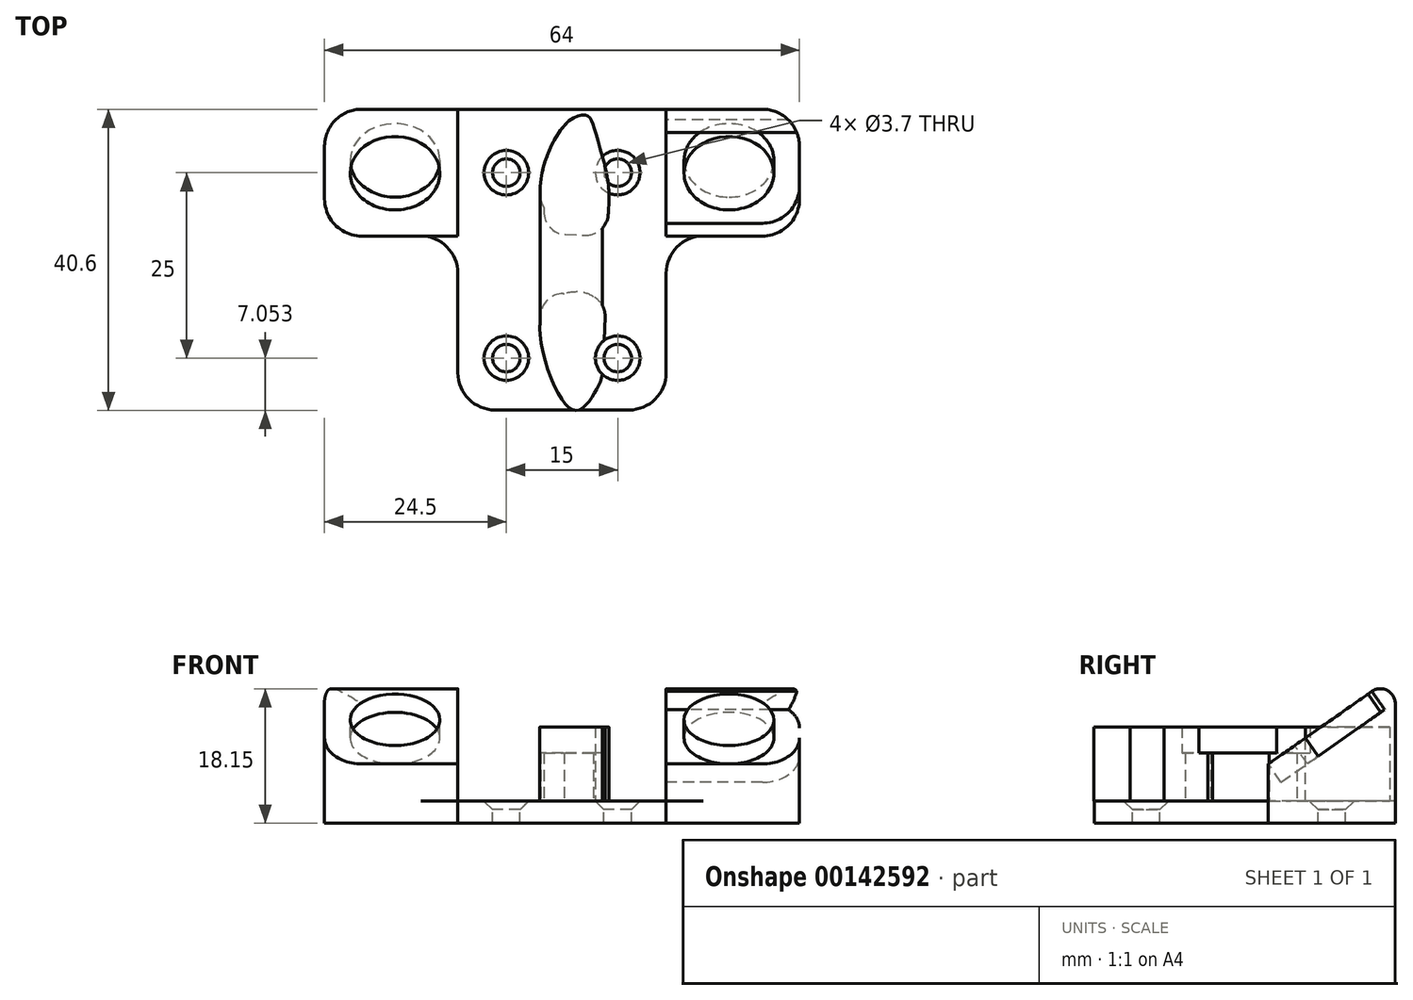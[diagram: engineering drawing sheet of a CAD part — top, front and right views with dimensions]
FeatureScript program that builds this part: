
annotation { "Feature Type Name" : "Feature", "Feature Type Description" : "" }
export const myFeature = defineFeature(function(context is Context, id is Id, definition is map)
    precondition{}
    {
        {
            var Q0;
            Q0=qCreatedBy(makeId("Top.planeOp"),FACE);
            var sketch = newSketch(context, id + "F0", { "sketchPlane" : qUnion([Q0])});
            skLineSegment(sketch, "E0.rect.top", {"start": v(-9.03, -25.17) * mm, "end": v(9.03, -25.17) * mm});
            skPoint(sketch, "E0.rect.middle", {"position": v(0, 0) * mm});
            skLineSegment(sketch, "E1.rect.bottom", {"start": v(27, 15.36) * mm, "end": v(-27, 15.36) * mm});
            skLineSegment(sketch, "E1.rect.top", {"start": v(27, -1.74) * mm, "end": v(19.03, -1.74) * mm});
            skLineSegment(sketch, "E1.rect.left", {"start": v(32, 15.36) * mm, "end": v(32, 15.36) * mm});
            skLineSegment(sketch, "E1.rect.right", {"start": v(-32, 10.36) * mm, "end": v(-32, 3.26) * mm});
            skPoint(sketch, "E1.rect.middle", {"position": v(0, 6.81) * mm});
            skLineSegment(sketch, "E2.trimOffspring", {"start": v(-19.03, -1.74) * mm, "end": v(-27, -1.74) * mm});
            skLineSegment(sketch, "E3", {"start": v(0, 6.81) * mm, "end": v(0, -18.19) * mm, "construction": true});
            skPoint(sketch, "E3.endSnap0", {"position": v(0, -25.17) * mm});
            skLineSegment(sketch, "E4", {"start": v(0, 6.81) * mm, "end": v(32, 6.81) * mm, "construction": true});
            skLineSegment(sketch, "E5", {"start": v(0, 6.81) * mm, "end": v(-32, 6.81) * mm, "construction": true});
            skPoint(sketch, "E6", {"position": v(7.5, 6.81) * mm});
            skLineSegment(sketch, "E7", {"start": v(7.5, 6.81) * mm, "end": v(7.5, -18.19) * mm, "construction": true});
            skPoint(sketch, "E8", {"position": v(7.5, -18.19) * mm});
            skPoint(sketch, "E9.MirrorP", {"position": v(-7.5, -18.19) * mm});
            skPoint(sketch, "E10.MirrorP", {"position": v(-7.5, 6.81) * mm});
            skCircle(sketch, "E11", {"center": v(-22.5, 6.81) * mm, "radius": 6.05 * mm, "construction": true});
            skCircle(sketch, "E12", {"center": v(22.5, 6.72) * mm, "radius": 6.05 * mm, "construction": true});
            skLineSegment(sketch, "E13", {"start": v(-7.5, 6.81) * mm, "end": v(-7.5, -18.19) * mm, "construction": true});
            skLineSegment(sketch, "E14", {"start": v(-7.5, -18.19) * mm, "end": v(7.5, -18.19) * mm, "construction": true});
            skPoint(sketch, "E15.orphan", {"position": v(0, -14.27) * mm});
            skPoint(sketch, "E16.orphan", {"position": v(0, 15.36) * mm});
            skLineSegment(sketch, "E17", {"start": v(14.03, -20.17) * mm, "end": v(14.03, -6.74) * mm});
            skLineSegment(sketch, "E18.MirrorCS", {"start": v(-14.03, -20.17) * mm, "end": v(-14.03, -6.74) * mm});
            skPoint(sketch, "E19.orphan", {"position": v(18, -25.17) * mm});
            skPoint(sketch, "E20.orphan", {"position": v(-18, -25.17) * mm});
            skLineSegment(sketch, "E21", {"start": v(14.03, -6.74) * mm, "end": v(14.03, 15.36) * mm});
            skLineSegment(sketch, "E22", {"start": v(32, -1.74) * mm, "end": v(32, -1.74) * mm});
            skLineSegment(sketch, "E23", {"start": v(32, 10.36) * mm, "end": v(32, 3.26) * mm});
            skLineSegment(sketch, "E24", {"start": v(14.03, 15.36) * mm, "end": v(14.03, 15.36) * mm});
            skLineSegment(sketch, "E25", {"start": v(-14.03, 15.36) * mm, "end": v(-14.03, 15.36) * mm});
            skLineSegment(sketch, "E26", {"start": v(-14.03, -6.74) * mm, "end": v(-14.03, 15.36) * mm});
            skLineSegment(sketch, "E27", {"start": v(-32, -1.74) * mm, "end": v(-32, -1.74) * mm});
            skLineSegment(sketch, "E28", {"start": v(-32, 15.36) * mm, "end": v(-32, 15.36) * mm});
            skArc(sketch, "E29.filletArc", {"start": v(19.03, -1.74) * mm, "mid": v(15.5, -3.2) * mm, "end": v(14.03, -6.74) * mm});
            skArc(sketch, "E30.filletArc", {"start": v(-14.03, -6.74) * mm, "mid": v(-15.5, -3.2) * mm, "end": v(-19.03, -1.74) * mm});
            skPoint(sketch, "E31.visualSharp", {"position": v(-14.03, -25.17) * mm});
            skArc(sketch, "E31.filletArc", {"start": v(-14.03, -20.17) * mm, "mid": v(-12.57, -23.7) * mm, "end": v(-9.03, -25.17) * mm});
            skPoint(sketch, "E32.visualSharp", {"position": v(14.03, -25.17) * mm});
            skArc(sketch, "E32.filletArc", {"start": v(9.03, -25.17) * mm, "mid": v(12.57, -23.7) * mm, "end": v(14.03, -20.17) * mm});
            skPoint(sketch, "E33.visualSharp", {"position": v(32, -1.74) * mm});
            skArc(sketch, "E33.filletArc", {"start": v(27, -1.74) * mm, "mid": v(30.54, -0.27) * mm, "end": v(32, 3.26) * mm});
            skPoint(sketch, "E34.visualSharp", {"position": v(32, 15.36) * mm});
            skArc(sketch, "E34.filletArc", {"start": v(32, 10.36) * mm, "mid": v(30.54, 13.9) * mm, "end": v(27, 15.36) * mm});
            skPoint(sketch, "E35.visualSharp", {"position": v(-32, 15.36) * mm});
            skArc(sketch, "E35.filletArc", {"start": v(-27, 15.36) * mm, "mid": v(-30.54, 13.9) * mm, "end": v(-32, 10.36) * mm});
            skPoint(sketch, "E36.visualSharp", {"position": v(-32, -1.74) * mm});
            skArc(sketch, "E36.filletArc", {"start": v(-32, 3.26) * mm, "mid": v(-30.54, -0.27) * mm, "end": v(-27, -1.74) * mm});
            skPoint(sketch, "E37.orphan", {"position": v(-14.03, -4.9) * mm});
            skPoint(sketch, "E38.orphan", {"position": v(14.03, -4.9) * mm});
            skLineSegment(sketch, "E39", {"start": v(-20.86, -1.74) * mm, "end": v(21.69, -1.74) * mm});
            skSolve(sketch);
        }
        {
            var Q0;
            Q0=makeQuery(id+"F0.imprint","IMPRINT",FACE,{"disambiguationData":[TD([[makeQuery(id+"F0.imprint","IMPRINT",EDGE,{"derivedFrom":sQuery(id+"F0.wireOp",EDGE,"E1.rect.right")}),1.0]])]});
            var Q1;
            Q1=makeQuery(id+"F0.imprint","IMPRINT",FACE,{"disambiguationData":[TD([[makeQuery(id+"F0.imprint","IMPRINT",EDGE,{"derivedFrom":sQuery(id+"F0.wireOp",EDGE,"E0.rect.top")}),1.0]])]});
            var Q2;
            Q2=makeQuery(id+"F0.imprint","IMPRINT",FACE,{"disambiguationData":[TD([[makeQuery(id+"F0.imprint","IMPRINT",EDGE,{"derivedFrom":sQuery(id+"F0.wireOp",EDGE,"E1.rect.top")}),-1.0]])]});
            var Q3;
            {var subQ0=sQuery(id+"F0.wireOp",EDGE,"E21");var subQ1=sQuery(id+"F0.wireOp",EDGE,"E1.rect.bottom");var subQ2=makeQuery(id+"F0.imprint","INTERSECT",VERTEX,{"derivedFrom":[subQ1,subQ0]});Q3=makeQuery(id+"F0.imprint","IMPRINT",FACE,{"disambiguationData":[TD([[makeQuery(id+"F0.imprint","IMPRINT",EDGE,{"disambiguationData":[TD([[subQ2,-1.0]])],"derivedFrom":subQ1}),1.0]])]});}
            var Q4;
            {var subQ0=sQuery(id+"F0.wireOp",EDGE,"E30.filletArc");Q4=makeQuery(id+"F0.imprint","IMPRINT",FACE,{"disambiguationData":[TD([[makeQuery(id+"F0.imprint","IMPRINT",EDGE,{"derivedFrom":subQ0}),-1.0]])]});}
            var Q5;
            {var subQ0=sQuery(id+"F0.wireOp",EDGE,"E29.filletArc");Q5=makeQuery(id+"F0.imprint","IMPRINT",FACE,{"disambiguationData":[TD([[makeQuery(id+"F0.imprint","IMPRINT",EDGE,{"derivedFrom":subQ0}),-1.0]])]});}
            extrude(context, id + "F1", {"entities" : qUnion([Q0, Q1, Q2, Q3, Q4, Q5]), "depth" : 3 * mm});
        }
        {
            var Q0;
            Q0=qCreatedBy(makeId("Right.planeOp"),FACE);
            var sketch = newSketch(context, id + "F2", { "sketchPlane" : qUnion([Q0])});
            skLineSegment(sketch, "E40.0", {"start": v(-1.74, 3) * mm, "end": v(-1.74, 0) * mm});
            skLineSegment(sketch, "E41.0", {"start": v(15.36, 3) * mm, "end": v(15.36, 0) * mm});
            skLineSegment(sketch, "E42", {"start": v(-1.74, 3) * mm, "end": v(15.36, 3) * mm});
            skLineSegment(sketch, "E43", {"start": v(15.36, 3) * mm, "end": v(15.36, 16.15) * mm});
            skLineSegment(sketch, "E44", {"start": v(-1.74, 3) * mm, "end": v(-1.74, 8) * mm});
            skLineSegment(sketch, "E45", {"start": v(-1.74, 8) * mm, "end": v(12.22, 17.8) * mm});
            skPoint(sketch, "E46.visualSharp", {"position": v(15.36, 20) * mm});
            skArc(sketch, "E46.filletArc", {"start": v(15.36, 16.15) * mm, "mid": v(14.29, 17.93) * mm, "end": v(12.22, 17.8) * mm});
            skSolve(sketch);
        }
        {
            var Q0;
            Q0=makeQuery(id+"F2.imprint","IMPRINT",FACE,{"disambiguationData":[TD([[makeQuery(id+"F2.imprint","IMPRINT",EDGE,{"derivedFrom":sQuery(id+"F2.wireOp",EDGE,"E42")}),1.0]])]});
            var Q1;
            Q1=makeQuery(id+"F1.opExtrude","SWEPT_FACE",FACE,{"disambiguationData":[OSD([sQuery(id+"F0.wireOp",EDGE,"E23")])]});
            var Q2;
            Q2=makeQuery(id+"F1.opExtrude","SWEPT_FACE",FACE,{"disambiguationData":[OSD([sQuery(id+"F0.wireOp",EDGE,"E1.rect.right")])]});
            extrude(context, id + "F3", {"entities" : qUnion([Q0]), "operationType" : NewBodyOperationType.ADD, "endBound" : BoundingType.UP_TO_SURFACE, "endBoundEntityFace" : qUnion([Q1]), "depth" : 25 * mm, "hasSecondDirection" : true, "secondDirectionBound" : SecondDirectionBoundingType.UP_TO_SURFACE, "secondDirectionOppositeDirection" : true, "secondDirectionBoundEntityFace" : qUnion([Q2]), "secondDirectionDepth" : 25 * mm});
        }
        {
            var Q0;
            {var subQ1=sQuery(id+"F2.wireOp",EDGE,"E42");Q0=makeQuery(id+"F3.boolean.opBoolean","SPLIT",FACE,{"disambiguationData":[TD([makeQuery(id+"F1.opExtrude","SWEPT_FACE",FACE,{"disambiguationData":[OSD([sQuery(id+"F0.wireOp",EDGE,"E35.filletArc")])]})])],"derivedFrom":makeQuery(id+"F3.opExtrude","SWEPT_FACE",FACE,{"disambiguationData":[OSD([subQ1])]})});}
            var Q1;
            {var subQ2=sQuery(id+"F2.wireOp",EDGE,"E42");Q1=makeQuery(id+"F3.boolean.opBoolean","SPLIT",FACE,{"disambiguationData":[TD([makeQuery(id+"F1.opExtrude","SWEPT_FACE",FACE,{"disambiguationData":[OSD([sQuery(id+"F0.wireOp",EDGE,"E36.filletArc")])]})])],"derivedFrom":makeQuery(id+"F3.opExtrude","SWEPT_FACE",FACE,{"disambiguationData":[OSD([subQ2])]})});}
            var Q2;
            {var subQ2=sQuery(id+"F2.wireOp",EDGE,"E42");Q2=makeQuery(id+"F3.boolean.opBoolean","SPLIT",FACE,{"disambiguationData":[TD([makeQuery(id+"F1.opExtrude","SWEPT_FACE",FACE,{"disambiguationData":[OSD([sQuery(id+"F0.wireOp",EDGE,"E33.filletArc")])]})])],"derivedFrom":makeQuery(id+"F3.opExtrude","SWEPT_FACE",FACE,{"disambiguationData":[OSD([subQ2])]})});}
            var Q3;
            {var subQ1=sQuery(id+"F2.wireOp",EDGE,"E42");Q3=makeQuery(id+"F3.boolean.opBoolean","SPLIT",FACE,{"disambiguationData":[TD([makeQuery(id+"F1.opExtrude","SWEPT_FACE",FACE,{"disambiguationData":[OSD([sQuery(id+"F0.wireOp",EDGE,"E34.filletArc")])]})])],"derivedFrom":makeQuery(id+"F3.opExtrude","SWEPT_FACE",FACE,{"disambiguationData":[OSD([subQ1])]})});}
            extrude(context, id + "F4", {"entities" : qUnion([Q0, Q1, Q2, Q3]), "operationType" : NewBodyOperationType.REMOVE, "oppositeDirection" : true, "depth" : 25 * mm});
        }
        {
            var Q0;
            Q0=makeQuery(id+"F3.opExtrude","SWEPT_FACE",FACE,{"disambiguationData":[OSD([sQuery(id+"F2.wireOp",EDGE,"E45")])]});
            var sketch = newSketch(context, id + "F5", { "sketchPlane" : qUnion([Q0])});
            skCircle(sketch, "E47", {"center": v(-22.5, 13.54) * mm, "radius": 6.05 * mm});
            skLineSegment(sketch, "E48.0", {"start": v(0, 23.81) * mm, "end": v(0, -14.89) * mm, "construction": true});
            skPoint(sketch, "E49.orphan", {"position": v(0, 5.58) * mm});
            skCircle(sketch, "E50.MirrorC", {"center": v(22.5, 13.54) * mm, "radius": 6.05 * mm});
            skLineSegment(sketch, "E51.0", {"start": v(14.03, 0) * mm, "end": v(14.03, 28.57) * mm});
            skLineSegment(sketch, "E52.0", {"start": v(-14.03, 0) * mm, "end": v(-14.03, 28.57) * mm});
            skPoint(sketch, "E53.orphan", {"position": v(-14.03, 12.58) * mm});
            skPoint(sketch, "E54.orphan", {"position": v(14.03, 12.58) * mm});
            skLineSegment(sketch, "E55", {"start": v(-14.03, 28.57) * mm, "end": v(14.09, 28.57) * mm});
            skPoint(sketch, "E56.orphan", {"position": v(14.03, -5.52) * mm});
            skPoint(sketch, "E57.orphan", {"position": v(-14.03, -5.52) * mm});
            skLineSegment(sketch, "E58", {"start": v(14.03, 0) * mm, "end": v(14.03, -5.02) * mm});
            skLineSegment(sketch, "E59", {"start": v(14.03, -5.02) * mm, "end": v(-14.03, -5.02) * mm});
            skLineSegment(sketch, "E60", {"start": v(-14.03, 0) * mm, "end": v(-14.03, -5.02) * mm});
            skSolve(sketch);
        }
        {
            var Q0;
            {var subQ0=sQuery(id+"F5.wireOp",EDGE,"E51.0");var subQ1=makeQuery(id+"F2.imprint","IMPRINT",EDGE,{"derivedFrom":sQuery(id+"F2.wireOp",EDGE,"E45")});var subQ2=makeQuery(id+"F3.opExtrude","TWEAK_EDGE",EDGE,{"derivedFrom":[makeQuery(id+"F2.imprint","IMPRINT",EDGE,{"derivedFrom":sQuery(id+"F2.wireOp",EDGE,"E44")}),subQ1]});var subQ3=makeQuery(id+"F5.imprint","INTERSECT",VERTEX,{"derivedFrom":[subQ2,subQ0]});Q0=makeQuery(id+"F5.imprint","IMPRINT",FACE,{"disambiguationData":[TD([[makeQuery(id+"F5.imprint","IMPRINT",EDGE,{"disambiguationData":[TD([[subQ3,-1.0]])],"derivedFrom":subQ0}),1.0]])]});}
            var Q1;
            {var subQ0=sQuery(id+"F5.wireOp",EDGE,"E58");Q1=makeQuery(id+"F5.imprint","IMPRINT",FACE,{"disambiguationData":[TD([[makeQuery(id+"F5.imprint","IMPRINT",EDGE,{"derivedFrom":subQ0}),-1.0]])]});}
            var Q2;
            {var subQ0=sQuery(id+"F5.wireOp",EDGE,"E55");var subQ1=sQuery(id+"F5.wireOp",EDGE,"E51.0");var subQ2=makeQuery(id+"F5.imprint","INTERSECT",VERTEX,{"derivedFrom":[subQ1,subQ0]});Q2=makeQuery(id+"F5.imprint","IMPRINT",FACE,{"disambiguationData":[TD([[makeQuery(id+"F5.imprint","IMPRINT",EDGE,{"disambiguationData":[TD([[subQ2,1.0]])],"derivedFrom":subQ0}),-1.0]])]});}
            var Q3;
            Q3=makeQuery(id+"F1.opExtrude","CAP_FACE",FACE,{"disambiguationData":[OSD([sQuery(id+"F0.wireOp",EDGE,"E0.rect.top"),sQuery(id+"F0.wireOp",EDGE,"E1.rect.bottom"),sQuery(id+"F0.wireOp",EDGE,"E1.rect.top"),sQuery(id+"F0.wireOp",EDGE,"E1.rect.right"),sQuery(id+"F0.wireOp",EDGE,"E2.trimOffspring"),sQuery(id+"F0.wireOp",EDGE,"E17"),sQuery(id+"F0.wireOp",EDGE,"E18.MirrorCS"),sQuery(id+"F0.wireOp",EDGE,"E23"),sQuery(id+"F0.wireOp",EDGE,"E29.filletArc"),sQuery(id+"F0.wireOp",EDGE,"E30.filletArc"),sQuery(id+"F0.wireOp",EDGE,"E31.filletArc"),sQuery(id+"F0.wireOp",EDGE,"E32.filletArc"),sQuery(id+"F0.wireOp",EDGE,"E33.filletArc"),sQuery(id+"F0.wireOp",EDGE,"E34.filletArc"),sQuery(id+"F0.wireOp",EDGE,"E35.filletArc"),sQuery(id+"F0.wireOp",EDGE,"E36.filletArc"),sQuery(id+"F0.wireOp",EDGE,"E39")])],"isStart":false});
            extrude(context, id + "F6", {"entities" : qUnion([Q0, Q1, Q2]), "operationType" : NewBodyOperationType.REMOVE, "endBound" : BoundingType.UP_TO_SURFACE, "oppositeDirection" : true, "endBoundEntityFace" : qUnion([Q3]), "depth" : 25 * mm});
        }
        {
            var Q0;
            Q0=makeQuery(id+"F5.imprint","IMPRINT",FACE,{"disambiguationData":[TD([[makeQuery(id+"F5.imprint","IMPRINT",EDGE,{"derivedFrom":sQuery(id+"F5.wireOp",EDGE,"E50.MirrorC")}),-1.0]])]});
            var Q1;
            Q1=makeQuery(id+"F5.imprint","IMPRINT",FACE,{"disambiguationData":[TD([[makeQuery(id+"F5.imprint","IMPRINT",EDGE,{"derivedFrom":sQuery(id+"F5.wireOp",EDGE,"E47")}),1.0]])]});
            extrude(context, id + "F7", {"entities" : qUnion([Q0, Q1]), "operationType" : NewBodyOperationType.REMOVE, "oppositeDirection" : true, "depth" : 3 * mm});
        }
        {
            var Q0;
            Q0=makeQuery(id+"F6.boolean.opBoolean","MERGE",FACE,{"derivedFrom":[makeQuery(id+"F1.opExtrude","CAP_FACE",FACE,{"disambiguationData":[OSD([sQuery(id+"F0.wireOp",EDGE,"E0.rect.top"),sQuery(id+"F0.wireOp",EDGE,"E1.rect.bottom"),sQuery(id+"F0.wireOp",EDGE,"E1.rect.top"),sQuery(id+"F0.wireOp",EDGE,"E1.rect.right"),sQuery(id+"F0.wireOp",EDGE,"E2.trimOffspring"),sQuery(id+"F0.wireOp",EDGE,"E17"),sQuery(id+"F0.wireOp",EDGE,"E18.MirrorCS"),sQuery(id+"F0.wireOp",EDGE,"E23"),sQuery(id+"F0.wireOp",EDGE,"E29.filletArc"),sQuery(id+"F0.wireOp",EDGE,"E30.filletArc"),sQuery(id+"F0.wireOp",EDGE,"E31.filletArc"),sQuery(id+"F0.wireOp",EDGE,"E32.filletArc"),sQuery(id+"F0.wireOp",EDGE,"E33.filletArc"),sQuery(id+"F0.wireOp",EDGE,"E34.filletArc"),sQuery(id+"F0.wireOp",EDGE,"E35.filletArc"),sQuery(id+"F0.wireOp",EDGE,"E36.filletArc"),sQuery(id+"F0.wireOp",EDGE,"E39")])],"isStart":false}),makeQuery(id+"F6.opExtrude","CAP_FACE",FACE,{"disambiguationData":[OSD([sQuery(id+"F5.wireOp",EDGE,"E51.0"),sQuery(id+"F5.wireOp",EDGE,"E52.0"),sQuery(id+"F5.wireOp",EDGE,"E55"),sQuery(id+"F5.wireOp",EDGE,"E58"),sQuery(id+"F5.wireOp",EDGE,"E59"),sQuery(id+"F5.wireOp",EDGE,"E60")])],"isStart":false})]});
            var sketch = newSketch(context, id + "F8", { "sketchPlane" : qUnion([Q0])});
            skLineSegment(sketch, "E61.0", {"start": v(7.5, 6.81) * mm, "end": v(7.5, -18.19) * mm, "construction": true});
            skLineSegment(sketch, "E62.0", {"start": v(-7.5, 6.81) * mm, "end": v(-7.5, -18.19) * mm, "construction": true});
            skPoint(sketch, "E63", {"position": v(7.5, -5.69) * mm});
            skLineSegment(sketch, "E64", {"start": v(7.5, -5.69) * mm, "end": v(-7.5, -5.69) * mm, "construction": true});
            skFitSpline(sketch, "E65", {"points": [v(3.44, 14.46) * mm, v(4.53, 12.17) * mm, v(6, 1.95) * mm, v(1.3, 0) * mm, v(-2.85, 3.22) * mm, v(0.62, 13.51) * mm, v(3.44, 14.46) * mm]});
            skPoint(sketch, "E66", {"position": v(6, 15.36) * mm});
            skArc(sketch, "E67", {"start": v(5.45, 9) * mm, "mid": v(4.55, 6.3) * mm, "end": v(6.32, 4.05) * mm});
            skPoint(sketch, "E68.MirrorP", {"position": v(6, -26.74) * mm});
            skPoint(sketch, "E69.trimOffspring.end.orphan", {"position": v(0, 15.36) * mm});
            skPoint(sketch, "E70.0.start.orphan", {"position": v(0, -1.74) * mm});
            skPoint(sketch, "E71.4.internal.snap0", {"position": v(0, -25.17) * mm});
            skFitSpline(sketch, "E71", {"points": [v(6.32, -15.43) * mm, v(4.76, -10.37) * mm, v(0, -9.59) * mm, v(-2.94, -13.26) * mm, v(0, -23.8) * mm, v(2.28, -25.17) * mm, v(4.46, -22.76) * mm, v(5.45, -20.38) * mm], "startDerivative": vector(-7.9, 22.48) * mm, "endDerivative": vector(4.5, 23.19) * mm});
            skLineSegment(sketch, "E72.left", {"start": v(-2.43, 2.12) * mm, "end": v(-2.44, 1.59) * mm});
            skLineSegment(sketch, "E72.right", {"start": v(6.32, 4.05) * mm, "end": v(6.24, 1.3) * mm});
            skLineSegment(sketch, "E73", {"start": v(0.43, -1.5) * mm, "end": v(3.11, -1.61) * mm});
            skLineSegment(sketch, "E74", {"start": v(0.17, -9.5) * mm, "end": v(2.86, -9.54) * mm});
            skLineSegment(sketch, "E75.trimOffspring", {"start": v(-2.87, -12.4) * mm, "end": v(-2.95, -15) * mm});
            skLineSegment(sketch, "E76.trimOffspring", {"start": v(5.8, -12.63) * mm, "end": v(5.71, -15.78) * mm});
            skPoint(sketch, "E77.visualSharp", {"position": v(-2.53, -1.38) * mm});
            skArc(sketch, "E77.filletArc", {"start": v(-2.44, 1.59) * mm, "mid": v(-1.64, -0.55) * mm, "end": v(0.43, -1.5) * mm});
            skPoint(sketch, "E78.visualSharp", {"position": v(6.14, -1.74) * mm});
            skArc(sketch, "E78.filletArc", {"start": v(3.11, -1.61) * mm, "mid": v(5.28, -0.81) * mm, "end": v(6.24, 1.3) * mm});
            skPoint(sketch, "E79.visualSharp", {"position": v(5.9, -9.59) * mm});
            skArc(sketch, "E79.filletArc", {"start": v(5.8, -12.63) * mm, "mid": v(4.98, -10.47) * mm, "end": v(2.86, -9.54) * mm});
            skPoint(sketch, "E80.visualSharp", {"position": v(-2.78, -9.45) * mm});
            skArc(sketch, "E80.filletArc", {"start": v(0.17, -9.5) * mm, "mid": v(-1.94, -10.33) * mm, "end": v(-2.87, -12.4) * mm});
            skArc(sketch, "E81", {"start": v(5.71, -15.78) * mm, "mid": v(4.5, -18.02) * mm, "end": v(5.45, -20.38) * mm});
            skSolve(sketch);
        }
        {
            var Q0;
            Q0=qSketchRegion(id+"F8",true);
            extrude(context, id + "F9", {"entities" : qUnion([Q0]), "operationType" : NewBodyOperationType.ADD, "depth" : 10 * mm});
        }
        {
            var Q0;
            Q0=sQuery(id+"F8.wireOp",VERTEX,"E62.0.start");
            var Q1;
            Q1=sQuery(id+"F8.wireOp",VERTEX,"E62.0.end");
            var Q2;
            Q2=sQuery(id+"F8.wireOp",VERTEX,"E67.center");
            var Q3;
            Q3=sQuery(id+"F8.wireOp",VERTEX,"7a332efa-baa1-4e39-bd40-679ceab8c39f0.MirrorCS.center");
            var Q4;
            Q4=sQuery(id+"F8.wireOp",VERTEX,"E61.0.end");
            var Q5;
            Q5=makeQuery(id+"F1.opExtrude","SWEPT_BODY",BODY,{"disambiguationData":[OSD([sQuery(id+"F0.wireOp",EDGE,"E0.rect.top"),sQuery(id+"F0.wireOp",EDGE,"E1.rect.bottom"),sQuery(id+"F0.wireOp",EDGE,"E1.rect.top"),sQuery(id+"F0.wireOp",EDGE,"E1.rect.right"),sQuery(id+"F0.wireOp",EDGE,"E2.trimOffspring"),sQuery(id+"F0.wireOp",EDGE,"E17"),sQuery(id+"F0.wireOp",EDGE,"E18.MirrorCS"),sQuery(id+"F0.wireOp",EDGE,"E23"),sQuery(id+"F0.wireOp",EDGE,"E29.filletArc"),sQuery(id+"F0.wireOp",EDGE,"E30.filletArc"),sQuery(id+"F0.wireOp",EDGE,"E31.filletArc"),sQuery(id+"F0.wireOp",EDGE,"E32.filletArc"),sQuery(id+"F0.wireOp",EDGE,"E33.filletArc"),sQuery(id+"F0.wireOp",EDGE,"E34.filletArc"),sQuery(id+"F0.wireOp",EDGE,"E35.filletArc"),sQuery(id+"F0.wireOp",EDGE,"E36.filletArc"),sQuery(id+"F0.wireOp",EDGE,"E39")])]});
            hole(context, id + "F10", {"style" : HoleStyle.C_SINK, "holeDiameter" : 3.7 * mm, "cSinkDiameter" : 6 * mm, "endStyle" : HoleEndStyle.THROUGH, "locations" : qUnion([Q0, Q1, Q2, Q3, Q4]), "scope" : qUnion([Q5]), "cSinkAngle" : 90 * degree});
        }
        {
            var Q0;
            Q0=qCreatedBy(makeId("Front.planeOp"),FACE);
            var sketch = newSketch(context, id + "F11", { "sketchPlane" : qUnion([Q0])});
            skLineSegment(sketch, "E82.0.3", {"start": v(5.45, 9.5) * mm, "end": v(5.45, 13) * mm});
            skFitSpline(sketch, "E82.0.4", {"points": [v(5.46, 13) * mm, v(2.65, 13) * mm, v(-0.15, 13) * mm, v(-2.95, 13) * mm]});
            skLineSegment(sketch, "E82.0.5", {"start": v(-2.95, 13) * mm, "end": v(-2.95, 9.5) * mm});
            skPoint(sketch, "E83", {"position": v(-2.95, 9.5) * mm});
            skLineSegment(sketch, "E84", {"start": v(-2.95, 9.5) * mm, "end": v(5.45, 9.5) * mm});
            skPoint(sketch, "E82.0.0.start.orphan", {"position": v(-2.95, 3) * mm});
            skPoint(sketch, "E82.0.2.end.orphan", {"position": v(5.45, 3) * mm});
            skPoint(sketch, "E82.0.1.end.orphan", {"position": v(2.28, 3) * mm});
            skPoint(sketch, "E82.0.1.start.orphan", {"position": v(1.5, 3) * mm});
            skSolve(sketch);
        }
        {
            var Q0;
            Q0=qSketchRegion(id+"F11",true);
            extrude(context, id + "F12", {"entities" : qUnion([Q0]), "operationType" : NewBodyOperationType.ADD, "depth" : 25 * mm});
        }
        {
            var Q0;
            {var subQ0=sQuery(id+"F11.wireOp",EDGE,"E82.0.5");var subQ1=sQuery(id+"F11.wireOp",EDGE,"E84");var subQ2=makeQuery(id+"F12.opExtrude","SWEPT_FACE",FACE,{"disambiguationData":[OSD([subQ1])]});Q0=makeQuery(id+"F12.boolean.opBoolean","SPLIT",FACE,{"disambiguationData":[TD([makeQuery(id+"F9.opExtrude","SWEPT_FACE",FACE,{"disambiguationData":[OSD([sQuery(id+"F8.wireOp",EDGE,"E71")])]}),makeQuery(id+"F9.opExtrude","SWEPT_FACE",FACE,{"disambiguationData":[OSD([sQuery(id+"F8.wireOp",EDGE,"E75.trimOffspring")])]}),makeQuery(id+"F12.opExtrude","CAP_FACE",FACE,{"disambiguationData":[OSD([sQuery(id+"F11.wireOp",EDGE,"E82.0.3"),sQuery(id+"F11.wireOp",EDGE,"E82.0.4"),subQ0,subQ1])],"isStart":false}),makeQuery(id+"F12.opExtrude","SWEPT_FACE",FACE,{"disambiguationData":[OSD([subQ0])]}),subQ2])],"derivedFrom":subQ2});}
            var Q1;
            {var subQ0=sQuery(id+"F11.wireOp",EDGE,"E84");var subQ1=sQuery(id+"F11.wireOp",EDGE,"E82.0.3");var subQ2=makeQuery(id+"F12.opExtrude","SWEPT_FACE",FACE,{"disambiguationData":[OSD([subQ0])]});Q1=makeQuery(id+"F12.boolean.opBoolean","SPLIT",FACE,{"disambiguationData":[TD([makeQuery(id+"F9.opExtrude","SWEPT_FACE",FACE,{"disambiguationData":[OSD([sQuery(id+"F8.wireOp",EDGE,"E71")])]}),makeQuery(id+"F9.opExtrude","SWEPT_FACE",FACE,{"disambiguationData":[OSD([sQuery(id+"F8.wireOp",EDGE,"E81")])]}),makeQuery(id+"F12.opExtrude","SWEPT_FACE",FACE,{"disambiguationData":[OSD([subQ1])]}),makeQuery(id+"F12.opExtrude","CAP_FACE",FACE,{"disambiguationData":[OSD([subQ1,sQuery(id+"F11.wireOp",EDGE,"E82.0.4"),sQuery(id+"F11.wireOp",EDGE,"E82.0.5"),subQ0])],"isStart":false}),subQ2])],"derivedFrom":subQ2});}
            var Q2;
            {var subQ0=makeQuery(id+"F12.opExtrude","SWEPT_FACE",FACE,{"disambiguationData":[OSD([sQuery(id+"F11.wireOp",EDGE,"E84")])]});Q2=makeQuery(id+"F12.boolean.opBoolean","SPLIT",FACE,{"disambiguationData":[TD([makeQuery(id+"F9.opExtrude","SWEPT_FACE",FACE,{"disambiguationData":[OSD([sQuery(id+"F8.wireOp",EDGE,"E71")])]}),makeQuery(id+"F9.opExtrude","SWEPT_FACE",FACE,{"disambiguationData":[OSD([sQuery(id+"F8.wireOp",EDGE,"E81")])]}),makeQuery(id+"F12.opExtrude","SWEPT_FACE",FACE,{"disambiguationData":[OSD([sQuery(id+"F11.wireOp",EDGE,"E82.0.3")])]}),subQ0])],"derivedFrom":subQ0});}
            extrude(context, id + "F13", {"entities" : qUnion([Q0, Q1, Q2]), "operationType" : NewBodyOperationType.REMOVE, "oppositeDirection" : true, "depth" : 25 * mm});
        }
        {
            var Q0;
            Q0=makeQuery(id+"F12.opExtrude","CAP_FACE",FACE,{"disambiguationData":[OSD([sQuery(id+"F11.wireOp",EDGE,"E82.0.3"),sQuery(id+"F11.wireOp",EDGE,"E82.0.4"),sQuery(id+"F11.wireOp",EDGE,"E82.0.5"),sQuery(id+"F11.wireOp",EDGE,"E84")])],"isStart":true});
            extrude(context, id + "F14", {"entities" : qUnion([Q0]), "operationType" : NewBodyOperationType.ADD, "depth" : 5 * mm});
        }
    });
